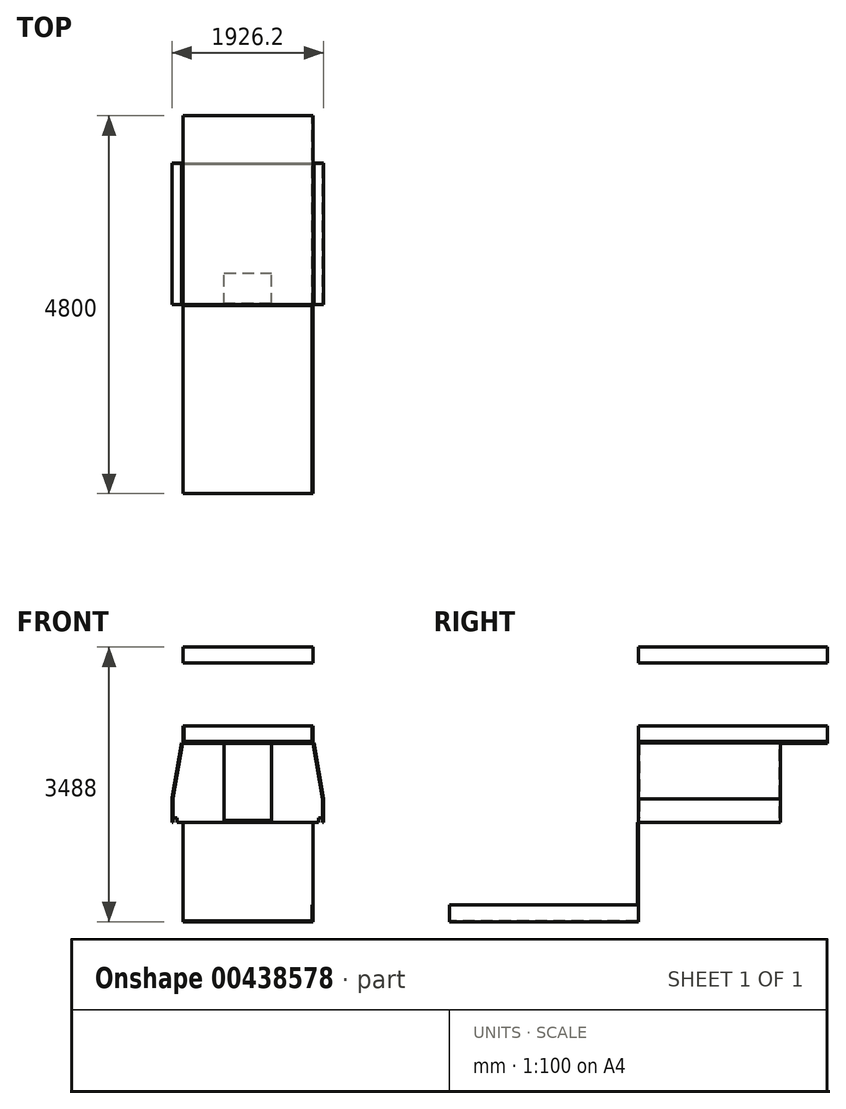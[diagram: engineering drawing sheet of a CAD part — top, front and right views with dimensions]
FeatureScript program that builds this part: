
annotation { "Feature Type Name" : "Feature", "Feature Type Description" : "" }
export const myFeature = defineFeature(function(context is Context, id is Id, definition is map)
    precondition{}
    {
        {
            var Q0;
            Q0=qCreatedBy(makeId("Front.planeOp"),FACE);
            var sketch = newSketch(context, id + "F0", { "sketchPlane" : qUnion([Q0])});
            skLineSegment(sketch, "E0", {"start": v(-950, -950) * mm, "end": v(-915, -950) * mm});
            skLineSegment(sketch, "E1", {"start": v(-915, -950) * mm, "end": v(-915, -1000) * mm});
            skLineSegment(sketch, "E2", {"start": v(-915, -1000) * mm, "end": v(915, -1000) * mm});
            skLineSegment(sketch, "E3", {"start": v(915, -1000) * mm, "end": v(915, -950) * mm});
            skLineSegment(sketch, "E4", {"start": v(915, -950) * mm, "end": v(950, -950) * mm});
            skSolve(sketch);
        }
        {
            var Q0;
            Q0=qCreatedBy(makeId("Front.planeOp"),FACE);
            var sketch = newSketch(context, id + "F1", { "sketchPlane" : qUnion([Q0])});
            skLineSegment(sketch, "E5", {"start": v(-950, -945) * mm, "end": v(-900, -945) * mm});
            skLineSegment(sketch, "E6", {"start": v(-900, -945) * mm, "end": v(-900, -1000) * mm});
            skLineSegment(sketch, "E7", {"start": v(-900, -1000) * mm, "end": v(900, -1000) * mm});
            skLineSegment(sketch, "E8", {"start": v(900, -1000) * mm, "end": v(900, -945) * mm});
            skLineSegment(sketch, "E9", {"start": v(900, -945) * mm, "end": v(950, -945) * mm});
            skLineSegment(sketch, "E10", {"start": v(-950, -945) * mm, "end": v(-950, -700.56) * mm});
            skLineSegment(sketch, "E11", {"start": v(-948.48, -683.2) * mm, "end": v(-827.13, 5) * mm});
            skLineSegment(sketch, "E12", {"start": v(-827.13, 5) * mm, "end": v(825.69, 5) * mm});
            skLineSegment(sketch, "E13", {"start": v(825.69, 5) * mm, "end": v(948.48, -691.38) * mm});
            skLineSegment(sketch, "E14", {"start": v(950, -708.75) * mm, "end": v(950, -945) * mm});
            skPoint(sketch, "E15.visualSharp", {"position": v(-950, -691.8) * mm});
            skArc(sketch, "E15.filletArc", {"start": v(-948.48, -683.2) * mm, "mid": v(-949.62, -691.84) * mm, "end": v(-950, -700.56) * mm});
            skPoint(sketch, "E16.visualSharp", {"position": v(950, -700) * mm});
            skArc(sketch, "E16.filletArc", {"start": v(950, -708.75) * mm, "mid": v(949.62, -700.03) * mm, "end": v(948.48, -691.38) * mm});
            skSolve(sketch);
        }
        {
            var Q0;
            Q0=makeQuery(id+"F1.imprint","IMPRINT",FACE,{"disambiguationData":[TD([[makeQuery(id+"F1.imprint","IMPRINT",EDGE,{"derivedFrom":sQuery(id+"F1.wireOp",EDGE,"E5")}),1.0]])]});
            extrude(context, id + "F2", {"entities" : qUnion([Q0]), "depth" : 13 * mm});
        }
        {
            var Q0;
            Q0=makeQuery(id+"F2.opExtrude","CAP_FACE",FACE,{"disambiguationData":[OSD([sQuery(id+"F1.wireOp",EDGE,"E5"),sQuery(id+"F1.wireOp",EDGE,"E6"),sQuery(id+"F1.wireOp",EDGE,"E7"),sQuery(id+"F1.wireOp",EDGE,"E8"),sQuery(id+"F1.wireOp",EDGE,"E9"),sQuery(id+"F1.wireOp",EDGE,"E10"),sQuery(id+"F1.wireOp",EDGE,"E11"),sQuery(id+"F1.wireOp",EDGE,"E12"),sQuery(id+"F1.wireOp",EDGE,"E13"),sQuery(id+"F1.wireOp",EDGE,"E14"),sQuery(id+"F1.wireOp",EDGE,"E15.filletArc"),sQuery(id+"F1.wireOp",EDGE,"E16.filletArc")])],"isStart":false});
            extrude(context, id + "F3", {"entities" : qUnion([Q0]), "oppositeDirection" : true, "depth" : 1800 * mm, "hasSecondDirection" : true, "secondDirectionOppositeDirection" : true, "secondDirectionDepth" : 1787 * mm});
        }
        {
            var Q0;
            Q0=qCreatedBy(makeId("Right.planeOp"),FACE);
            var sketch = newSketch(context, id + "F4", { "sketchPlane" : qUnion([Q0])});
            skLineSegment(sketch, "E17.bottom", {"start": v(-13, 5) * mm, "end": v(2387, 5) * mm});
            skLineSegment(sketch, "E17.top", {"start": v(-13, 25) * mm, "end": v(2387, 25) * mm});
            skLineSegment(sketch, "E17.left", {"start": v(-13, 5) * mm, "end": v(-13, 25) * mm});
            skLineSegment(sketch, "E17.right", {"start": v(2387, 5) * mm, "end": v(2387, 25) * mm});
            skSolve(sketch);
        }
        {
            var Q0;
            Q0 = qSketchRegion(id + "F4", true);
            extrude(context, id + "F5", {"entities" : qUnion([Q0]), "endBound" : BoundingType.SYMMETRIC, "depth" : 25 * mm, "offsetDistance" : 25 * mm});
        }
        {
            var Q0;
            Q0=makeQuery(id+"F4.imprint","IMPRINT",FACE,{"disambiguationData":[TD([[makeQuery(id+"F4.imprint","IMPRINT",EDGE,{"derivedFrom":sQuery(id+"F4.wireOp",EDGE,"E17.bottom")}),1.0]])]});
            extrude(context, id + "F6", {"entities" : qUnion([Q0]), "endBound" : BoundingType.SYMMETRIC, "depth" : 1650 * mm, "offsetDistance" : 25 * mm});
        }
        {
            var Q0;
            Q0=makeQuery(id+"F6.opExtrude","SWEPT_FACE",FACE,{"disambiguationData":[OSD([sQuery(id+"F4.wireOp",EDGE,"E17.top")])]});
            var sketch = newSketch(context, id + "F7", { "sketchPlane" : qUnion([Q0])});
            skLineSegment(sketch, "E18.bottom", {"start": v(825.69, -13) * mm, "end": v(812.69, -13) * mm});
            skLineSegment(sketch, "E18.top", {"start": v(825, 2387) * mm, "end": v(812, 2387) * mm});
            skLineSegment(sketch, "E18.left", {"start": v(825.69, -13) * mm, "end": v(825, 2387) * mm});
            skLineSegment(sketch, "E18.right", {"start": v(812.69, -13) * mm, "end": v(812, 2387) * mm});
            skLineSegment(sketch, "E19.bottom", {"start": v(-825, -13) * mm, "end": v(-812, -13) * mm});
            skLineSegment(sketch, "E19.top", {"start": v(-825, 2387) * mm, "end": v(-812, 2387) * mm});
            skLineSegment(sketch, "E19.left", {"start": v(-825, -13) * mm, "end": v(-825, 2387) * mm});
            skLineSegment(sketch, "E19.right", {"start": v(-812, -13) * mm, "end": v(-812, 2387) * mm});
            skLineSegment(sketch, "E20.left", {"start": v(-825, 2387) * mm, "end": v(-825, 2387) * mm});
            skLineSegment(sketch, "E20.right", {"start": v(812, 2387) * mm, "end": v(825, 2387) * mm});
            skLineSegment(sketch, "E21.bottom", {"start": v(812, 2387) * mm, "end": v(-812, 2387) * mm});
            skLineSegment(sketch, "E21.top", {"start": v(812, 2374) * mm, "end": v(-812, 2374) * mm});
            skLineSegment(sketch, "E21.left", {"start": v(812, 2387) * mm, "end": v(812, 2374) * mm});
            skLineSegment(sketch, "E21.right", {"start": v(-812, 2387) * mm, "end": v(-812, 2374) * mm});
            skSolve(sketch);
        }
        {
            var Q0;
            Q0 = qSketchRegion(id + "F7", true);
            extrude(context, id + "F8", {"entities" : qUnion([Q0]), "operationType" : NewBodyOperationType.ADD, "depth" : 200 * mm, "offsetDistance" : 25 * mm});
        }
        {
            var Q0;
            Q0=qCreatedBy(makeId("Right.planeOp"),FACE);
            var sketch = newSketch(context, id + "F9", { "sketchPlane" : qUnion([Q0])});
            skLineSegment(sketch, "E22.bottom", {"start": v(2387, 1225) * mm, "end": v(-13, 1225) * mm});
            skLineSegment(sketch, "E22.top", {"start": v(2387, 1025) * mm, "end": v(-13, 1025) * mm});
            skLineSegment(sketch, "E22.left", {"start": v(2387, 1225) * mm, "end": v(2387, 1025) * mm});
            skLineSegment(sketch, "E22.right", {"start": v(-13, 1225) * mm, "end": v(-13, 1025) * mm});
            skSolve(sketch);
        }
        {
            var Q0;
            Q0 = qSketchRegion(id + "F9", true);
            extrude(context, id + "F10", {"entities" : qUnion([Q0]), "endBound" : BoundingType.SYMMETRIC, "depth" : 1650 * mm, "offsetDistance" : 25 * mm});
        }
        {
            var Q0;
            Q0=qCreatedBy(makeId("Right.planeOp"),FACE);
            var sketch = newSketch(context, id + "F11", { "sketchPlane" : qUnion([Q0])});
            skLineSegment(sketch, "E23.bottom", {"start": v(-26, -1000) * mm, "end": v(-13, -1000) * mm});
            skLineSegment(sketch, "E23.top", {"start": v(-26, -2250) * mm, "end": v(-13, -2250) * mm});
            skLineSegment(sketch, "E23.left", {"start": v(-26, -1000) * mm, "end": v(-26, -2250) * mm});
            skLineSegment(sketch, "E23.right", {"start": v(-13, -1000) * mm, "end": v(-13, -2250) * mm});
            skLineSegment(sketch, "E24.bottom", {"start": v(-13, -2250) * mm, "end": v(-2413, -2250) * mm});
            skLineSegment(sketch, "E24.top", {"start": v(-13, -2263) * mm, "end": v(-2413, -2263) * mm});
            skLineSegment(sketch, "E24.left", {"start": v(-13, -2250) * mm, "end": v(-13, -2263) * mm});
            skLineSegment(sketch, "E24.right", {"start": v(-2413, -2250) * mm, "end": v(-2413, -2263) * mm});
            skSolve(sketch);
        }
        {
            var Q0;
            Q0 = qSketchRegion(id + "F11", true);
            extrude(context, id + "F12", {"entities" : qUnion([Q0]), "endBound" : BoundingType.SYMMETRIC, "depth" : 1650 * mm, "offsetDistance" : 25 * mm});
        }
        {
            var Q0;
            Q0=makeQuery(id+"F3.opExtrude","CAP_FACE",FACE,{"disambiguationData":[OSD([sQuery(id+"F1.wireOp",EDGE,"E5"),sQuery(id+"F1.wireOp",EDGE,"E6"),sQuery(id+"F1.wireOp",EDGE,"E7"),sQuery(id+"F1.wireOp",EDGE,"E8"),sQuery(id+"F1.wireOp",EDGE,"E9"),sQuery(id+"F1.wireOp",EDGE,"E10"),sQuery(id+"F1.wireOp",EDGE,"E11"),sQuery(id+"F1.wireOp",EDGE,"E12"),sQuery(id+"F1.wireOp",EDGE,"E13"),sQuery(id+"F1.wireOp",EDGE,"E14"),sQuery(id+"F1.wireOp",EDGE,"E15.filletArc"),sQuery(id+"F1.wireOp",EDGE,"E16.filletArc")])],"isStart":false});
            var sketch = newSketch(context, id + "F13", { "sketchPlane" : qUnion([Q0])});
            skLineSegment(sketch, "E25.bottom", {"start": v(950, -1000) * mm, "end": v(963, -1000) * mm});
            skLineSegment(sketch, "E25.top", {"start": v(950, -691.84) * mm, "end": v(963, -691.84) * mm});
            skLineSegment(sketch, "E25.left", {"start": v(950, -1000) * mm, "end": v(950, -691.84) * mm});
            skLineSegment(sketch, "E25.right", {"start": v(963, -1000) * mm, "end": v(963, -691.84) * mm});
            skLineSegment(sketch, "E26.bottom", {"start": v(963, -691.84) * mm, "end": v(950, -691.84) * mm});
            skLineSegment(sketch, "E26.top", {"start": v(839.74, 7.22) * mm, "end": v(827.13, 5) * mm});
            skLineSegment(sketch, "E26.left", {"start": v(963, -691.84) * mm, "end": v(839.74, 7.22) * mm});
            skLineSegment(sketch, "E26.right", {"start": v(950, -691.84) * mm, "end": v(827.13, 5) * mm});
            skLineSegment(sketch, "E27.bottom", {"start": v(-950, -1000) * mm, "end": v(-963, -1000) * mm});
            skLineSegment(sketch, "E27.top", {"start": v(-950, -700.56) * mm, "end": v(-963, -700.56) * mm});
            skLineSegment(sketch, "E27.left", {"start": v(-950, -1000) * mm, "end": v(-950, -700.56) * mm});
            skLineSegment(sketch, "E27.right", {"start": v(-963, -1000) * mm, "end": v(-963, -700.56) * mm});
            skLineSegment(sketch, "E28.bottom", {"start": v(-963, -700.56) * mm, "end": v(-950, -700.56) * mm});
            skLineSegment(sketch, "E28.top", {"start": v(-837.8, 7.27) * mm, "end": v(-825, 5) * mm});
            skLineSegment(sketch, "E28.left", {"start": v(-963.2, -700.56) * mm, "end": v(-837.8, 7.27) * mm});
            skLineSegment(sketch, "E28.right", {"start": v(-950, -700.56) * mm, "end": v(-825, 5) * mm});
            skLineSegment(sketch, "E29", {"start": v(-963.2, -700.56) * mm, "end": v(-963, -700.56) * mm});
            skSolve(sketch);
        }
        {
            var Q0;
            Q0 = qSketchRegion(id + "F13", true);
            extrude(context, id + "F14", {"entities" : qUnion([Q0]), "depth" : -1800 * mm, "offsetDistance" : 25 * mm});
        }
        {
            var Q0;
            Q0=makeQuery(id+"F12.opExtrude","CAP_FACE",FACE,{"disambiguationData":[OSD([sQuery(id+"F11.wireOp",EDGE,"E23.bottom"),sQuery(id+"F11.wireOp",EDGE,"E23.left"),sQuery(id+"F11.wireOp",EDGE,"E23.right"),sQuery(id+"F11.wireOp",EDGE,"E24.bottom"),sQuery(id+"F11.wireOp",EDGE,"E24.top"),sQuery(id+"F11.wireOp",EDGE,"E24.left"),sQuery(id+"F11.wireOp",EDGE,"E24.right")])],"isStart":false});
            var sketch = newSketch(context, id + "F15", { "sketchPlane" : qUnion([Q0])});
            skLineSegment(sketch, "E30.bottom", {"start": v(-26, -2250) * mm, "end": v(-2413, -2250) * mm});
            skLineSegment(sketch, "E30.top", {"start": v(-26, -2050) * mm, "end": v(-2413, -2050) * mm});
            skLineSegment(sketch, "E30.left", {"start": v(-26, -2250) * mm, "end": v(-26, -2050) * mm});
            skLineSegment(sketch, "E30.right", {"start": v(-2413, -2250) * mm, "end": v(-2413, -2050) * mm});
            skSolve(sketch);
        }
        {
            var Q0;
            Q0=makeQuery(id+"F15.imprint","IMPRINT",FACE,{"disambiguationData":[TD([[makeQuery(id+"F15.imprint","IMPRINT",EDGE,{"derivedFrom":sQuery(id+"F15.wireOp",EDGE,"E30.bottom")}),-1.0]])]});
            extrude(context, id + "F16", {"entities" : qUnion([Q0]), "operationType" : NewBodyOperationType.ADD, "oppositeDirection" : true, "depth" : 13 * mm, "offsetDistance" : 25 * mm});
        }
        {
            var Q0;
            Q0=makeQuery(id+"F6.opExtrude","SWEPT_FACE",FACE,{"disambiguationData":[OSD([sQuery(id+"F4.wireOp",EDGE,"E17.top")])]});
            var sketch = newSketch(context, id + "F17", { "sketchPlane" : qUnion([Q0])});
            skLineSegment(sketch, "E31.bottom", {"start": v(-300, -13) * mm, "end": v(300, -13) * mm});
            skLineSegment(sketch, "E31.top", {"start": v(-300, 387) * mm, "end": v(300, 387) * mm});
            skLineSegment(sketch, "E31.left", {"start": v(-300, -13) * mm, "end": v(-300, 387) * mm});
            skLineSegment(sketch, "E31.right", {"start": v(300, -13) * mm, "end": v(300, 387) * mm});
            skSolve(sketch);
        }
        {
            var Q0;
            Q0 = qSketchRegion(id + "F17", true);
            extrude(context, id + "F18", {"entities" : qUnion([Q0]), "operationType" : NewBodyOperationType.REMOVE, "oppositeDirection" : true, "depth" : 1000 * mm, "offsetDistance" : 25 * mm});
        }
    });
